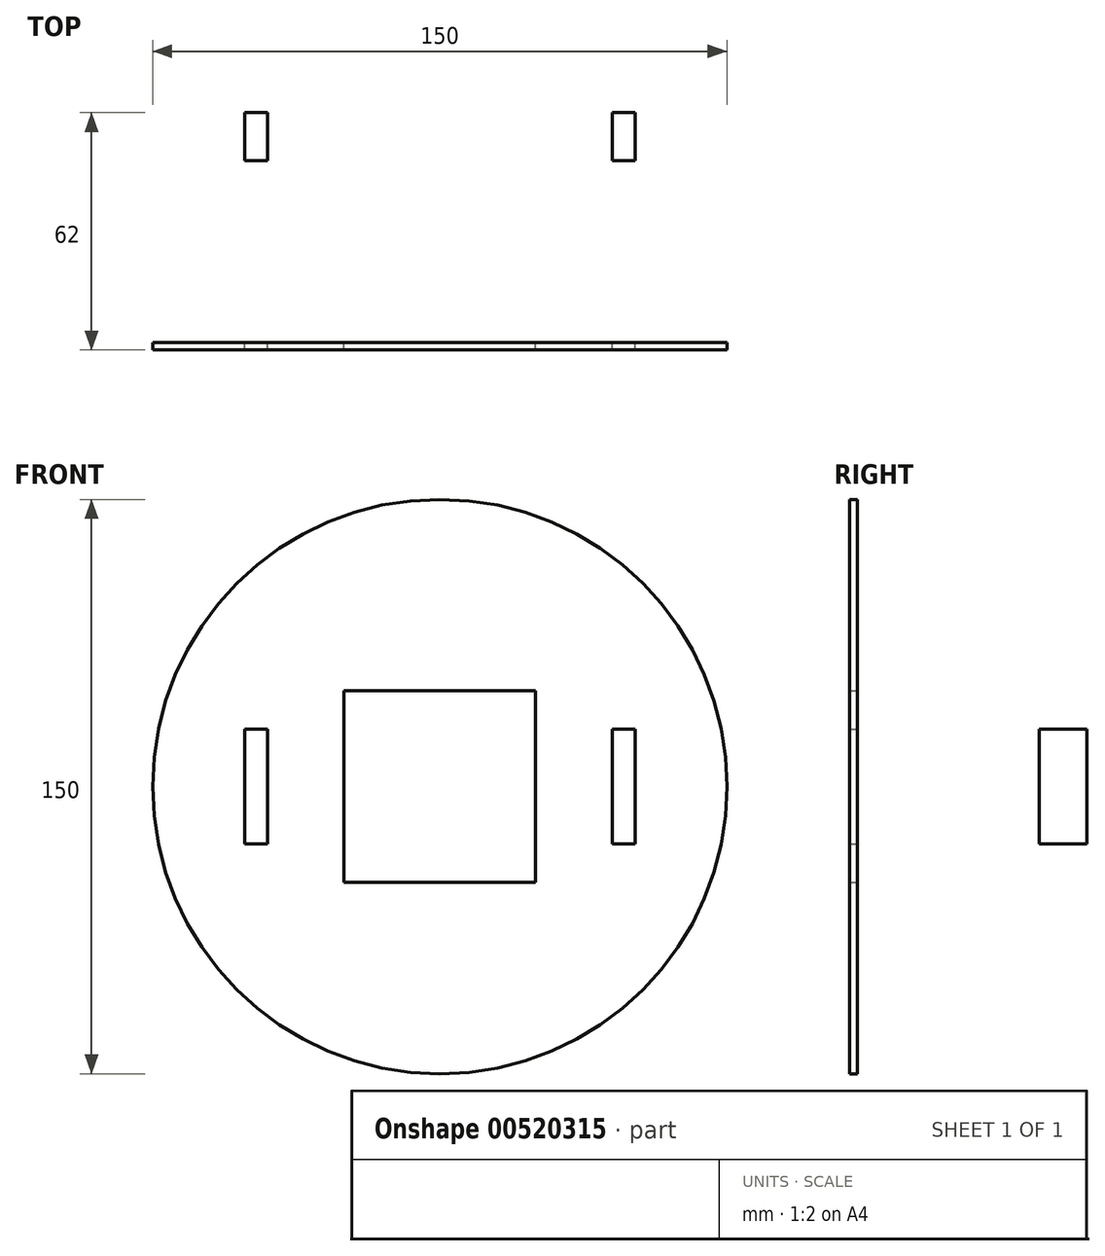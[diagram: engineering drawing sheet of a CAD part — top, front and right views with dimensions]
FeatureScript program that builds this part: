
annotation { "Feature Type Name" : "Feature", "Feature Type Description" : "" }
export const myFeature = defineFeature(function(context is Context, id is Id, definition is map)
    precondition{}
    {
        {
            var Q0;
            Q0=qCreatedBy(makeId("Front.planeOp"),FACE);
            var sketch = newSketch(context, id + "F0", { "sketchPlane" : qUnion([Q0])});
            skCircle(sketch, "E0", {"center": v(0, 0) * mm, "radius": 75 * mm});
            skLineSegment(sketch, "E1", {"start": v(-25, 25) * mm, "end": v(25, 25) * mm});
            skLineSegment(sketch, "E2", {"start": v(25, 25) * mm, "end": v(25, -25) * mm});
            skLineSegment(sketch, "E3", {"start": v(25, -25) * mm, "end": v(-25, -25) * mm});
            skLineSegment(sketch, "E4", {"start": v(-25, -25) * mm, "end": v(-25, 25) * mm});
            skLineSegment(sketch, "E5", {"start": v(-45, 0) * mm, "end": v(-45, -15) * mm});
            skLineSegment(sketch, "E6", {"start": v(-45, -15) * mm, "end": v(-51, -15) * mm});
            skLineSegment(sketch, "E7", {"start": v(-51, -15) * mm, "end": v(-51, 15) * mm});
            skLineSegment(sketch, "E8", {"start": v(-51, 15) * mm, "end": v(-45, 15) * mm});
            skLineSegment(sketch, "E9", {"start": v(-45, 15) * mm, "end": v(-45, 0) * mm});
            skLineSegment(sketch, "E10", {"start": v(45, 0) * mm, "end": v(45, -15) * mm});
            skLineSegment(sketch, "E11", {"start": v(45, -15) * mm, "end": v(51, -15) * mm});
            skLineSegment(sketch, "E12", {"start": v(51, -15) * mm, "end": v(51, 15) * mm});
            skLineSegment(sketch, "E13", {"start": v(51, 15) * mm, "end": v(45, 15) * mm});
            skLineSegment(sketch, "E14", {"start": v(45, 15) * mm, "end": v(45, 0) * mm});
            skSolve(sketch);
        }
        {
            var Q0;
            Q0=qCreatedBy(makeId("Front.planeOp"),FACE);
            cPlane(context, id + "F1", {"entities" : qUnion([Q0]), "cplaneType" : CPlaneType.OFFSET, "offset" : 60 * mm, "width" : 150 * mm, "height" : 150 * mm});
        }
        {
            var Q0;
            Q0=qCreatedBy(id+"F1.planeOp",FACE);
            var sketch = newSketch(context, id + "F2", { "sketchPlane" : qUnion([Q0])});
            skCircle(sketch, "E15", {"center": v(0, 0) * mm, "radius": 75 * mm});
            skLineSegment(sketch, "E16", {"start": v(-25, 25) * mm, "end": v(25, 25) * mm});
            skLineSegment(sketch, "E17", {"start": v(25, 25) * mm, "end": v(25, -25) * mm});
            skLineSegment(sketch, "E18", {"start": v(25, -25) * mm, "end": v(-25, -25) * mm});
            skLineSegment(sketch, "E19", {"start": v(-25, -25) * mm, "end": v(-25, 25) * mm});
            skLineSegment(sketch, "E20", {"start": v(-45, 0) * mm, "end": v(-45, -15) * mm});
            skLineSegment(sketch, "E21", {"start": v(-45, -15) * mm, "end": v(-51, -15) * mm});
            skLineSegment(sketch, "E22", {"start": v(-51, -15) * mm, "end": v(-51, 15) * mm});
            skLineSegment(sketch, "E23", {"start": v(-51, 15) * mm, "end": v(-45, 15) * mm});
            skLineSegment(sketch, "E24", {"start": v(-45, 15) * mm, "end": v(-45, 0) * mm});
            skLineSegment(sketch, "E25", {"start": v(45, 0) * mm, "end": v(45, -15) * mm});
            skLineSegment(sketch, "E26", {"start": v(45, -15) * mm, "end": v(51, -15) * mm});
            skLineSegment(sketch, "E27", {"start": v(51, -15) * mm, "end": v(51, 15) * mm});
            skLineSegment(sketch, "E28", {"start": v(51, 15) * mm, "end": v(45, 15) * mm});
            skLineSegment(sketch, "E29", {"start": v(45, 15) * mm, "end": v(45, 0) * mm});
            skSolve(sketch);
        }
        {
            var Q0;
            Q0=makeQuery(id+"F2.imprint","IMPRINT",FACE,{"disambiguationData":[TD([[makeQuery(id+"F2.imprint","IMPRINT",EDGE,{"derivedFrom":sQuery(id+"F2.wireOp",EDGE,"E15")}),1.0]])]});
            extrude(context, id + "F3", {"entities" : qUnion([Q0]), "depth" : 2 * mm, "offsetDistance" : 25 * mm});
        }
        {
            var Q0;
            Q0=makeQuery(id+"F0.imprint","IMPRINT",FACE,{"disambiguationData":[TD([[makeQuery(id+"F0.imprint","IMPRINT",EDGE,{"derivedFrom":sQuery(id+"F0.wireOp",EDGE,"E5")}),-1.0]])]});
            var Q1;
            Q1=makeQuery(id+"F0.imprint","IMPRINT",FACE,{"disambiguationData":[TD([[makeQuery(id+"F0.imprint","IMPRINT",EDGE,{"derivedFrom":sQuery(id+"F0.wireOp",EDGE,"E10")}),1.0]])]});
            extrude(context, id + "F4", {"entities" : qUnion([Q0, Q1]), "depth" : 12.5 * mm, "offsetDistance" : 25 * mm});
        }
    });
